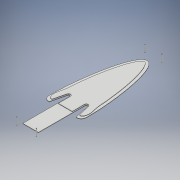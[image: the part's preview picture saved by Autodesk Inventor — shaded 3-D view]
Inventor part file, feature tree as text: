
AUTODESK INVENTOR PART (.ipt)
format: ipt  version: 2019.3 (Build 233278000, 278)  size: 5,854,720 bytes
history: native  units: mm
features: other x3, extrude x3, sketch x3, mirror x1
ambient origin geometry x8: Origin, YZ Plane, XZ Plane, XY Plane, X Axis, Y Axis, Z Axis, Center Point
bodies: Solid5 (feature_tree)
feature tree (10):
  other  "RearFenderOuter"
  extrude  "Extrusion3"  Depth=3.0mm TaperAngle=0.0deg
  extrude  "Extrusion5"  Depth=5.0mm
  extrude  "Extrusion6"  Depth=50.0mm TaperAngle=0.0deg
  mirror  "Mirror2"
  sketch  "Sketch2"  dims[d13=830.0mm d59=3.0mm d60=0.0mm]
  other  "Image1"
  sketch  "Sketch8"  dims[d63=3.0mm d64=0.0mm d65=5.0mm]
  other  "RearFenderInner"
  sketch  "Sketch9"  dims[d66=5.0mm d67=50.0mm d68=0.0mm d69=60.0mm d70=70.0mm]
